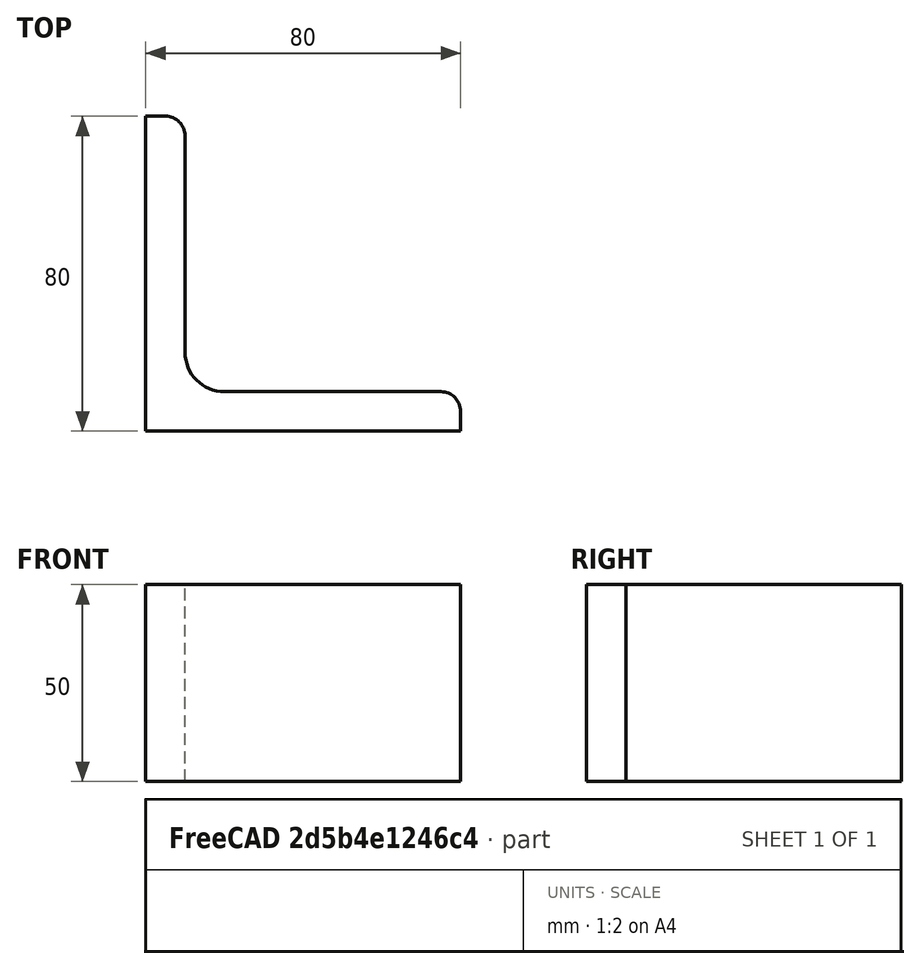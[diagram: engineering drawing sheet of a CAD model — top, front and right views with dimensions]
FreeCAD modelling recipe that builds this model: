
FCSTD DOCUMENT  (FreeCAD 0.15R4671 (Git))
Label: Angle Bar L80x80x10 EN10056 S235JR
License: All rights reserved
LicenseURL: http://en.wikipedia.org/wiki/All_rights_reserved
objects: Sketcher::SketchObject×1, Part::Extrusion×1
note: 2 computed .brp shape members not serialized (recipe doc carries the construction recipe); baked Part::Feature solids carry a one-line shape summary decoded from their .brp

FEATURE [Sketcher::SketchObject] Sketch
  sketch-geometry (9):
    g0: LineSegment StartX=0 StartY=0 StartZ=0 EndX=80 EndY=0 EndZ=0
    g1: LineSegment StartX=80 StartY=0 StartZ=0 EndX=80 EndY=5 EndZ=0
    g2: LineSegment StartX=75 StartY=10 StartZ=0 EndX=20 EndY=10 EndZ=0
    g3: LineSegment StartX=0 StartY=0 StartZ=0 EndX=0 EndY=80 EndZ=0
    g4: LineSegment StartX=0 StartY=80 StartZ=0 EndX=5 EndY=80 EndZ=0
    g5: LineSegment StartX=10 StartY=75 StartZ=0 EndX=10 EndY=20 EndZ=0
    g6: ArcOfCircle CenterX=20 CenterY=20 CenterZ=0 NormalX=0 NormalY=0 NormalZ=1 Radius=10 StartAngle=3.14159 EndAngle=4.71239
    g7: ArcOfCircle CenterX=5 CenterY=75 CenterZ=0 NormalX=0 NormalY=0 NormalZ=1 Radius=5 StartAngle=0 EndAngle=1.5708
    g8: ArcOfCircle CenterX=75 CenterY=5 CenterZ=0 NormalX=0 NormalY=0 NormalZ=1 Radius=5 StartAngle=0 EndAngle=1.5708
  constraints (23):
    c: Coincident(g0,g-1)
    c: Horizontal(g0)
    c: Coincident(g1,g0)
    c: Vertical(g1)
    c: Horizontal(g2)
    c: Coincident(g3,g-1)
    c: Vertical(g3)
    c: Coincident(g4,g3)
    c: Horizontal(g4)
    c: Vertical(g5)
    c: Tangent(g5,g6) = -1.5708
    c: Tangent(g2,g6) = 1.5708
    c: Tangent(g4,g7) = 1.5708
    c: Tangent(g5,g7) = 1.5708
    c: Tangent(g2,g8) = -1.5708
    c: Tangent(g1,g8) = -1.5708
    c: DistanceX(g0) = 80
    c: DistanceY(g3) = 80
    c: DistanceY(g0,g2) = 10
    c: DistanceX(g3,g5) = 10
    c: Radius(g6) = 10
    c: Radius(g8) = 5
    c: Radius(g7) = 5
FEATURE [Part::Extrusion] Extrude  label="Angle Bar L80x80x10 EN10056 S235JR"
  Base = -> Sketch
  Dir = (0,0,50)
  Solid = true
